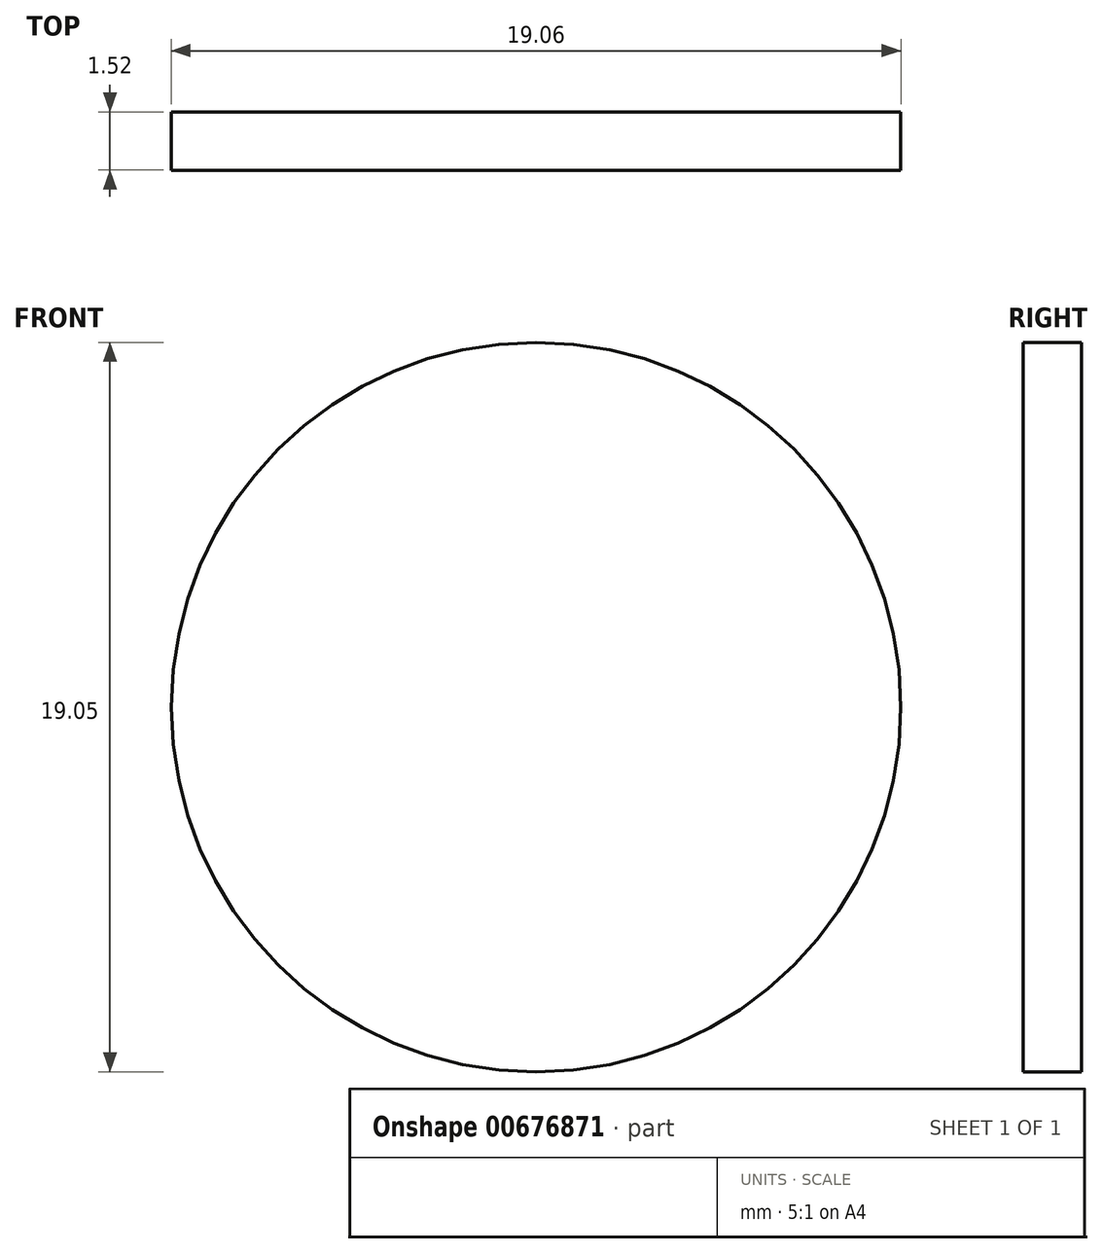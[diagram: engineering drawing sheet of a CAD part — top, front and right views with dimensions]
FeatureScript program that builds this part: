
annotation { "Feature Type Name" : "Feature", "Feature Type Description" : "" }
export const myFeature = defineFeature(function(context is Context, id is Id, definition is map)
    precondition{}
    {
        {
            var Q0;
            Q0=qCreatedBy(makeId("Front.planeOp"),FACE);
            var sketch = newSketch(context, id + "F0", { "sketchPlane" : qUnion([Q0])});
            skCircle(sketch, "E0", {"center": v(0, 0.07) * mm, "radius": 9.53 * mm});
            skSolve(sketch);
        }
        {
            var Q0;
            Q0=makeQuery(id+"F0.imprint","IMPRINT",FACE,{"disambiguationData":[TD([[makeQuery(id+"F0.imprint","IMPRINT",EDGE,{"derivedFrom":sQuery(id+"F0.wireOp",EDGE,"E0")}),1.0]])]});
            extrude(context, id + "F1", {"entities" : qUnion([Q0]), "depth" : 1.52 * mm, "offsetDistance" : 25.4 * mm});
        }
    });
